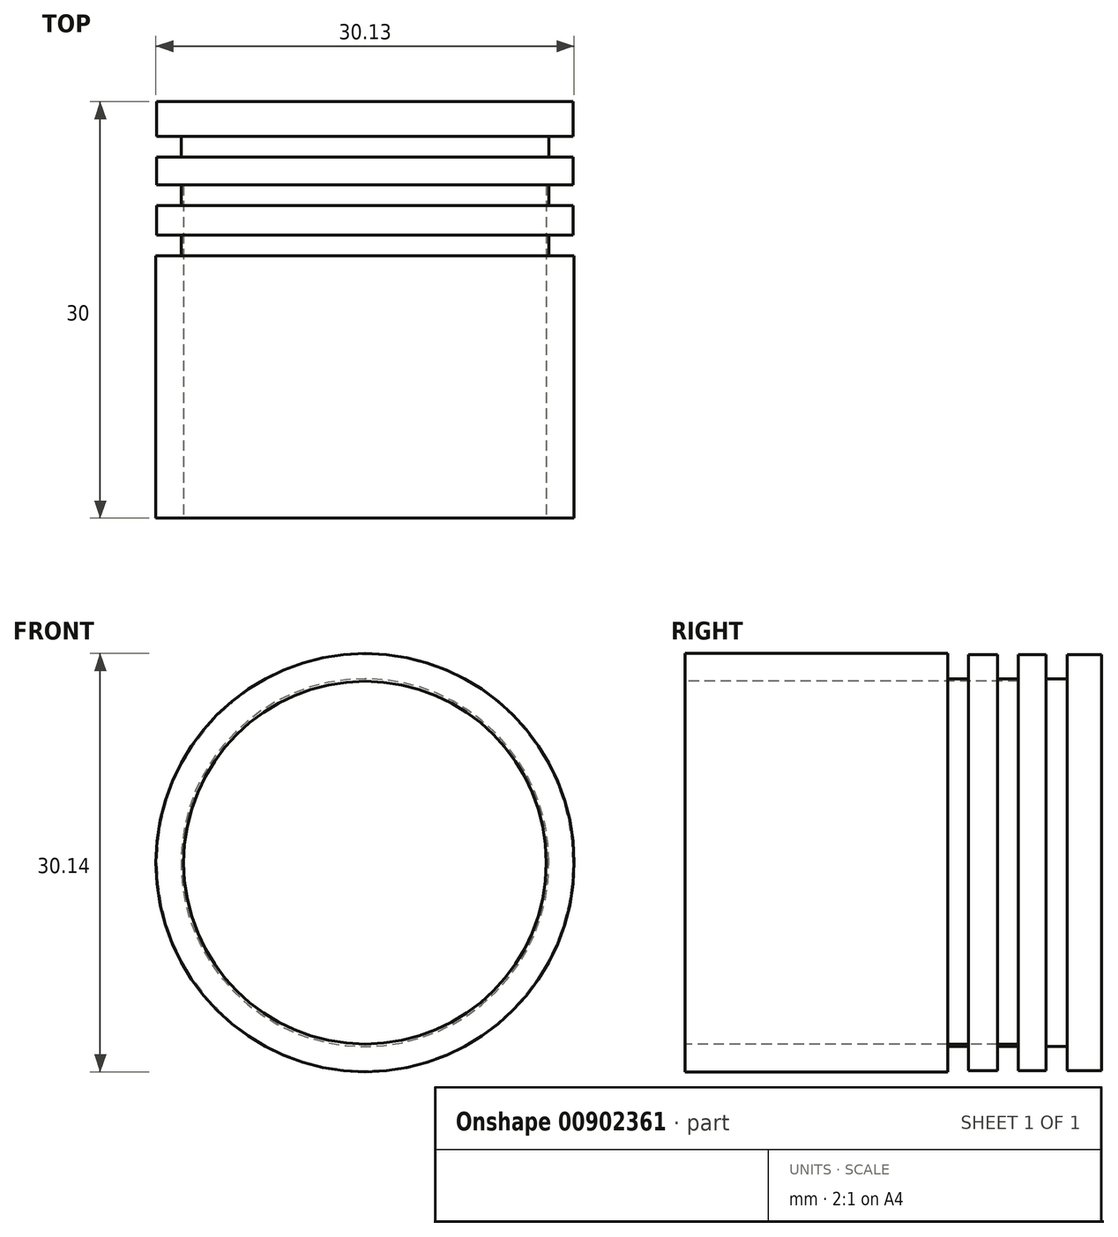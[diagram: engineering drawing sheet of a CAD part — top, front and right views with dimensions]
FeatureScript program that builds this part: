
annotation { "Feature Type Name" : "Feature", "Feature Type Description" : "" }
export const myFeature = defineFeature(function(context is Context, id is Id, definition is map)
    precondition{}
    {
        {
            var Q0;
            Q0=qCreatedBy(makeId("Top.planeOp"),FACE);
            var sketch = newSketch(context, id + "F0", { "sketchPlane" : qUnion([Q0])});
            skLineSegment(sketch, "E0.MirrorCS", {"start": v(-17.21, 22.28) * mm, "end": v(-17.21, 20.18) * mm});
            skLineSegment(sketch, "E1.MirrorCS", {"start": v(-18.96, 20.18) * mm, "end": v(-18.96, 18.68) * mm});
            skLineSegment(sketch, "E2.MirrorCS", {"start": v(-17.15, 18.68) * mm, "end": v(-17.15, 16.68) * mm});
            skLineSegment(sketch, "E3.MirrorCS", {"start": v(-17.15, 4.52) * mm, "end": v(-17.15, -0.22) * mm});
            skLineSegment(sketch, "E4.MirrorCS", {"start": v(-17.21, 27.28) * mm, "end": v(-17.21, 29.78) * mm});
            skLineSegment(sketch, "E5.MirrorCS", {"start": v(-17.21, 25.78) * mm, "end": v(-17.21, 23.78) * mm});
            skLineSegment(sketch, "E6", {"start": v(-17.15, 18.68) * mm, "end": v(-32.21, 18.68) * mm});
            skLineSegment(sketch, "E7", {"start": v(-17.21, 20.18) * mm, "end": v(-32.21, 20.18) * mm});
            skLineSegment(sketch, "E8", {"start": v(-17.21, 22.28) * mm, "end": v(-32.21, 22.28) * mm});
            skLineSegment(sketch, "E9", {"start": v(-17.21, 23.78) * mm, "end": v(-32.21, 23.78) * mm});
            skLineSegment(sketch, "E10", {"start": v(-17.21, 25.78) * mm, "end": v(-32.21, 25.78) * mm});
            skLineSegment(sketch, "E11", {"start": v(-17.21, 27.28) * mm, "end": v(-32.21, 27.28) * mm});
            skLineSegment(sketch, "E12", {"start": v(-17.21, 29.78) * mm, "end": v(-32.21, 29.78) * mm});
            skLineSegment(sketch, "E13", {"start": v(-17.15, 16.68) * mm, "end": v(-17.15, 4.52) * mm});
            skLineSegment(sketch, "E14", {"start": v(-17.15, 16.68) * mm, "end": v(-20.65, 16.68) * mm});
            skLineSegment(sketch, "E15", {"start": v(-20.65, 16.68) * mm, "end": v(-20.65, 17.38) * mm});
            skLineSegment(sketch, "E16", {"start": v(-20.65, 17.38) * mm, "end": v(-21.65, 17.38) * mm});
            skLineSegment(sketch, "E17", {"start": v(-21.65, 17.38) * mm, "end": v(-21.65, 16.68) * mm});
            skLineSegment(sketch, "E18", {"start": v(-21.65, 16.68) * mm, "end": v(-25.85, 16.68) * mm});
            skLineSegment(sketch, "E19", {"start": v(-25.85, 16.68) * mm, "end": v(-32.21, 16.68) * mm});
            skLineSegment(sketch, "E20", {"start": v(-18.96, 22.28) * mm, "end": v(-18.96, 23.78) * mm});
            skLineSegment(sketch, "E21", {"start": v(-18.96, 25.78) * mm, "end": v(-18.96, 27.28) * mm});
            skLineSegment(sketch, "E22", {"start": v(-32.21, 1.53) * mm, "end": v(-32.21, 29.78) * mm});
            skLineSegment(sketch, "E23", {"start": v(-17.15, -0.22) * mm, "end": v(-19.15, -0.22) * mm});
            skLineSegment(sketch, "E24", {"start": v(-19.15, -0.22) * mm, "end": v(-19.15, 1.53) * mm});
            skLineSegment(sketch, "E25", {"start": v(-32.21, 1.53) * mm, "end": v(-19.15, 1.53) * mm});
            skSolve(sketch);
        }
        {
            var Q0;
            Q0=makeQuery(id+"F0.imprint","IMPRINT",FACE,{"disambiguationData":[TD([[makeQuery(id+"F0.imprint","IMPRINT",EDGE,{"derivedFrom":sQuery(id+"F0.wireOp",EDGE,"E3.MirrorCS")}),-1.0]])]});
            var Q1;
            {var subQ2=sQuery(id+"F0.wireOp",EDGE,"E2.MirrorCS");Q1=makeQuery(id+"F0.imprint","IMPRINT",FACE,{"disambiguationData":[TD([[makeQuery(id+"F0.imprint","IMPRINT",EDGE,{"derivedFrom":subQ2}),-1.0]])]});}
            var Q2;
            {var subQ6=sQuery(id+"F0.wireOp",EDGE,"E0.MirrorCS");Q2=makeQuery(id+"F0.imprint","IMPRINT",FACE,{"disambiguationData":[TD([[makeQuery(id+"F0.imprint","IMPRINT",EDGE,{"derivedFrom":subQ6}),-1.0]])]});}
            var Q3;
            {var subQ0=sQuery(id+"F0.wireOp",EDGE,"E1.MirrorCS");Q3=makeQuery(id+"F0.imprint","IMPRINT",FACE,{"disambiguationData":[TD([[makeQuery(id+"F0.imprint","IMPRINT",EDGE,{"derivedFrom":subQ0}),-1.0]])]});}
            var Q4;
            {var subQ3=sQuery(id+"F0.wireOp",EDGE,"E20");Q4=makeQuery(id+"F0.imprint","IMPRINT",FACE,{"disambiguationData":[TD([[makeQuery(id+"F0.imprint","IMPRINT",EDGE,{"derivedFrom":subQ3}),1.0]])]});}
            var Q5;
            {var subQ1=sQuery(id+"F0.wireOp",EDGE,"E5.MirrorCS");Q5=makeQuery(id+"F0.imprint","IMPRINT",FACE,{"disambiguationData":[TD([[makeQuery(id+"F0.imprint","IMPRINT",EDGE,{"derivedFrom":subQ1}),-1.0]])]});}
            var Q6;
            {var subQ3=sQuery(id+"F0.wireOp",EDGE,"E21");Q6=makeQuery(id+"F0.imprint","IMPRINT",FACE,{"disambiguationData":[TD([[makeQuery(id+"F0.imprint","IMPRINT",EDGE,{"derivedFrom":subQ3}),1.0]])]});}
            var Q7;
            {var subQ5=sQuery(id+"F0.wireOp",EDGE,"E4.MirrorCS");Q7=makeQuery(id+"F0.imprint","IMPRINT",FACE,{"disambiguationData":[TD([[makeQuery(id+"F0.imprint","IMPRINT",EDGE,{"derivedFrom":subQ5}),1.0]])]});}
            var Q8;
            Q8=sQuery(id+"F0.wireOp",EDGE,"E22");
            revolve(context, id + "F1", {"surfaceOperationType" : NewSurfaceOperationType.NEW, "entities" : qUnion([Q0, Q1, Q2, Q3, Q4, Q5, Q6, Q7]), "axis" : qUnion([Q8]), "revolveType" : RevolveType.FULL});
        }
        {
            var Q0;
            Q0=makeQuery(id+"F1.opRevolve","SWEPT_FACE",FACE,{"disambiguationData":[OSD([sQuery(id+"F0.wireOp",EDGE,"E25")])]});
            extrude(context, id + "F2", {"entities" : qUnion([Q0]), "operationType" : NewBodyOperationType.REMOVE, "oppositeDirection" : true, "depth" : 22.25 * mm, "offsetDistance" : 25 * mm});
        }
    });
